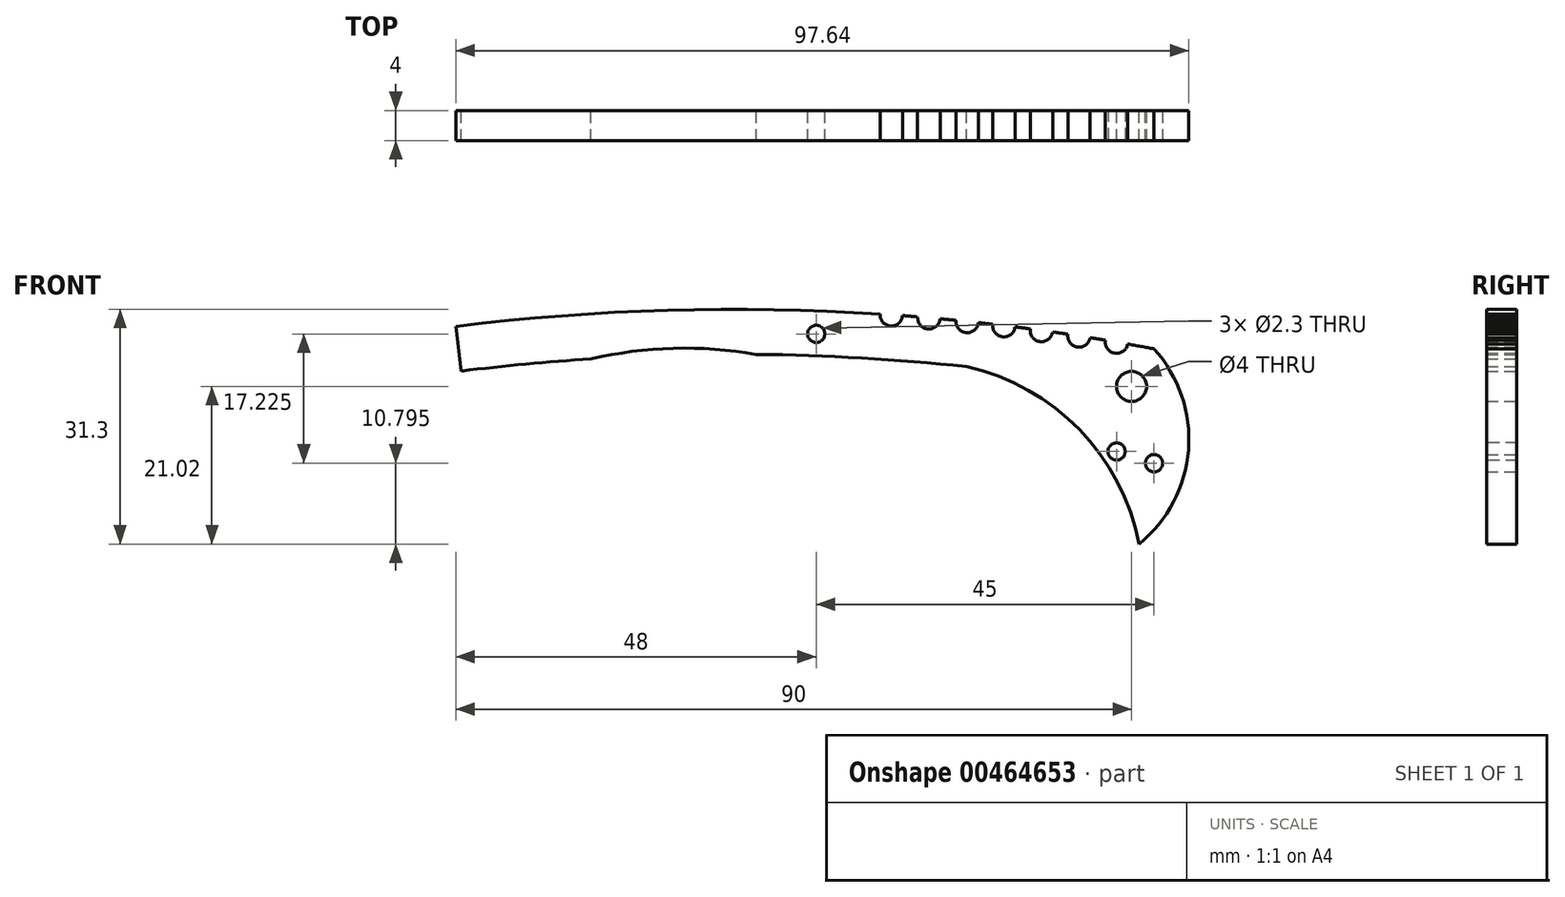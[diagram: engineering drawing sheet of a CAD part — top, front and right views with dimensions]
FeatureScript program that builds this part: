
annotation { "Feature Type Name" : "Feature", "Feature Type Description" : "" }
export const myFeature = defineFeature(function(context is Context, id is Id, definition is map)
    precondition{}
    {
        {
            var Q0;
            Q0=qCreatedBy(makeId("Front.planeOp"),FACE);
            var sketch = newSketch(context, id + "F0", { "sketchPlane" : qUnion([Q0])});
            skArc(sketch, "E0", {"start": v(85, 9) * mm, "mid": v(83.24, 9.33) * mm, "end": v(81.48, 9.65) * mm});
            skArc(sketch, "E1", {"start": v(80, -19) * mm, "mid": v(89.36, -6.22) * mm, "end": v(85, 9) * mm});
            skArc(sketch, "E2.0", {"start": v(60, 6.64) * mm, "mid": v(46.02, 7.79) * mm, "end": v(32, 8.27) * mm});
            skArc(sketch, "E3", {"start": v(83, -17.02) * mm, "mid": v(75.04, -1.74) * mm, "end": v(60, 6.64) * mm});
            skLineSegment(sketch, "E4", {"start": v(-8, 12) * mm, "end": v(-7.26, 6.05) * mm});
            skArc(sketch, "E5", {"start": v(48.5, 13.65) * mm, "mid": v(49.9, 12.05) * mm, "end": v(51.5, 13.43) * mm});
            skArc(sketch, "E6", {"start": v(58.6, 12.81) * mm, "mid": v(59.95, 11.17) * mm, "end": v(61.6, 12.5) * mm});
            skArc(sketch, "E7", {"start": v(53.5, 13.28) * mm, "mid": v(54.87, 11.66) * mm, "end": v(56.5, 13.02) * mm});
            skArc(sketch, "E8", {"start": v(63.51, 12.29) * mm, "mid": v(64.82, 10.62) * mm, "end": v(66.49, 11.93) * mm});
            skArc(sketch, "E9", {"start": v(68.51, 11.66) * mm, "mid": v(69.8, 9.98) * mm, "end": v(71.49, 11.25) * mm});
            skArc(sketch, "E10", {"start": v(73.52, 10.95) * mm, "mid": v(74.77, 9.25) * mm, "end": v(76.48, 10.5) * mm});
            skArc(sketch, "E11", {"start": v(78.52, 10.16) * mm, "mid": v(79.74, 8.43) * mm, "end": v(81.48, 9.65) * mm});
            skArc(sketch, "E12.trimOffspring", {"start": v(48.5, 13.65) * mm, "mid": v(20.21, 14.16) * mm, "end": v(-8, 12) * mm});
            skArc(sketch, "E13.trimOffspring", {"start": v(53.5, 13.28) * mm, "mid": v(52.5, 13.36) * mm, "end": v(51.5, 13.43) * mm});
            skArc(sketch, "E14.trimOffspring", {"start": v(58.6, 12.81) * mm, "mid": v(57.55, 12.92) * mm, "end": v(56.5, 13.02) * mm});
            skArc(sketch, "E15.trimOffspring", {"start": v(63.51, 12.29) * mm, "mid": v(62.55, 12.4) * mm, "end": v(61.6, 12.5) * mm});
            skArc(sketch, "E16.trimOffspring", {"start": v(68.51, 11.66) * mm, "mid": v(67.5, 11.8) * mm, "end": v(66.49, 11.93) * mm});
            skArc(sketch, "E17.trimOffspring", {"start": v(73.52, 10.95) * mm, "mid": v(72.5, 11.1) * mm, "end": v(71.49, 11.25) * mm});
            skArc(sketch, "E18.trimOffspring", {"start": v(78.52, 10.16) * mm, "mid": v(77.5, 10.33) * mm, "end": v(76.48, 10.5) * mm});
            skCircle(sketch, "E19", {"center": v(40, 11) * mm, "radius": 1.15 * mm});
            skArc(sketch, "E20", {"start": v(32, 8.27) * mm, "mid": v(20.97, 9.08) * mm, "end": v(10, 7.67) * mm});
            skArc(sketch, "E21.trimOffspring", {"start": v(10, 7.67) * mm, "mid": v(1.36, 6.99) * mm, "end": v(-7.26, 6.05) * mm});
            skCircle(sketch, "E22", {"center": v(82, 4) * mm, "radius": 2 * mm});
            skCircle(sketch, "E23", {"center": v(85, -6.22) * mm, "radius": 1.15 * mm});
            skSolve(sketch);
        }
        {
            var Q0;
            Q0 = qSketchRegion(id + "F0", true);
            extrude(context, id + "F1", {"entities" : qUnion([Q0]), "depth" : 4 * mm});
        }
        {
            var Q0;
            Q0=makeQuery(id+"F1.opExtrude","CAP_FACE",FACE,{"disambiguationData":[OSD([sQuery(id+"F0.wireOp",EDGE,"E0"),sQuery(id+"F0.wireOp",EDGE,"E1"),sQuery(id+"F0.wireOp",EDGE,"E2.0"),sQuery(id+"F0.wireOp",EDGE,"E3"),sQuery(id+"F0.wireOp",EDGE,"E4"),sQuery(id+"F0.wireOp",EDGE,"E5"),sQuery(id+"F0.wireOp",EDGE,"E6"),sQuery(id+"F0.wireOp",EDGE,"E7"),sQuery(id+"F0.wireOp",EDGE,"E8"),sQuery(id+"F0.wireOp",EDGE,"E9"),sQuery(id+"F0.wireOp",EDGE,"E10"),sQuery(id+"F0.wireOp",EDGE,"E11"),sQuery(id+"F0.wireOp",EDGE,"E12.trimOffspring"),sQuery(id+"F0.wireOp",EDGE,"E13.trimOffspring"),sQuery(id+"F0.wireOp",EDGE,"E14.trimOffspring"),sQuery(id+"F0.wireOp",EDGE,"E15.trimOffspring"),sQuery(id+"F0.wireOp",EDGE,"E16.trimOffspring"),sQuery(id+"F0.wireOp",EDGE,"E17.trimOffspring"),sQuery(id+"F0.wireOp",EDGE,"E18.trimOffspring"),sQuery(id+"F0.wireOp",EDGE,"E19"),sQuery(id+"F0.wireOp",EDGE,"E20"),sQuery(id+"F0.wireOp",EDGE,"E21.trimOffspring"),sQuery(id+"F0.wireOp",EDGE,"E22"),sQuery(id+"F0.wireOp",EDGE,"E23")])],"isStart":false});
            var sketch = newSketch(context, id + "F2", { "sketchPlane" : qUnion([Q0])});
            skCircle(sketch, "E24", {"center": v(80, -4.68) * mm, "radius": 1.15 * mm});
            skPoint(sketch, "E25", {"position": v(77.5, -4.62) * mm});
            skSolve(sketch);
        }
        {
            var Q0;
            Q0=sQuery(id+"F2.wireOp",VERTEX,"E24.center");
            var Q1;
            Q1=makeQuery(id+"F1.opExtrude","SWEPT_BODY",BODY,{"disambiguationData":[OSD([sQuery(id+"F0.wireOp",EDGE,"E0"),sQuery(id+"F0.wireOp",EDGE,"E1"),sQuery(id+"F0.wireOp",EDGE,"E2.0"),sQuery(id+"F0.wireOp",EDGE,"E3"),sQuery(id+"F0.wireOp",EDGE,"E4"),sQuery(id+"F0.wireOp",EDGE,"E5"),sQuery(id+"F0.wireOp",EDGE,"E6"),sQuery(id+"F0.wireOp",EDGE,"E7"),sQuery(id+"F0.wireOp",EDGE,"E8"),sQuery(id+"F0.wireOp",EDGE,"E9"),sQuery(id+"F0.wireOp",EDGE,"E10"),sQuery(id+"F0.wireOp",EDGE,"E11"),sQuery(id+"F0.wireOp",EDGE,"E12.trimOffspring"),sQuery(id+"F0.wireOp",EDGE,"E13.trimOffspring"),sQuery(id+"F0.wireOp",EDGE,"E14.trimOffspring"),sQuery(id+"F0.wireOp",EDGE,"E15.trimOffspring"),sQuery(id+"F0.wireOp",EDGE,"E16.trimOffspring"),sQuery(id+"F0.wireOp",EDGE,"E17.trimOffspring"),sQuery(id+"F0.wireOp",EDGE,"E18.trimOffspring"),sQuery(id+"F0.wireOp",EDGE,"E19"),sQuery(id+"F0.wireOp",EDGE,"E20"),sQuery(id+"F0.wireOp",EDGE,"E21.trimOffspring"),sQuery(id+"F0.wireOp",EDGE,"E22"),sQuery(id+"F0.wireOp",EDGE,"E23")])]});
            hole(context, id + "F3", {"style" : HoleStyle.SIMPLE, "endStyle" : HoleEndStyle.THROUGH, "holeDiameter" : 2.3 * mm, "isTappedThrough" : true, "tappedDepth" : 12 * mm, "tapClearance" : 3, "locations" : qUnion([Q0]), "scope" : qUnion([Q1])});
        }
    });
